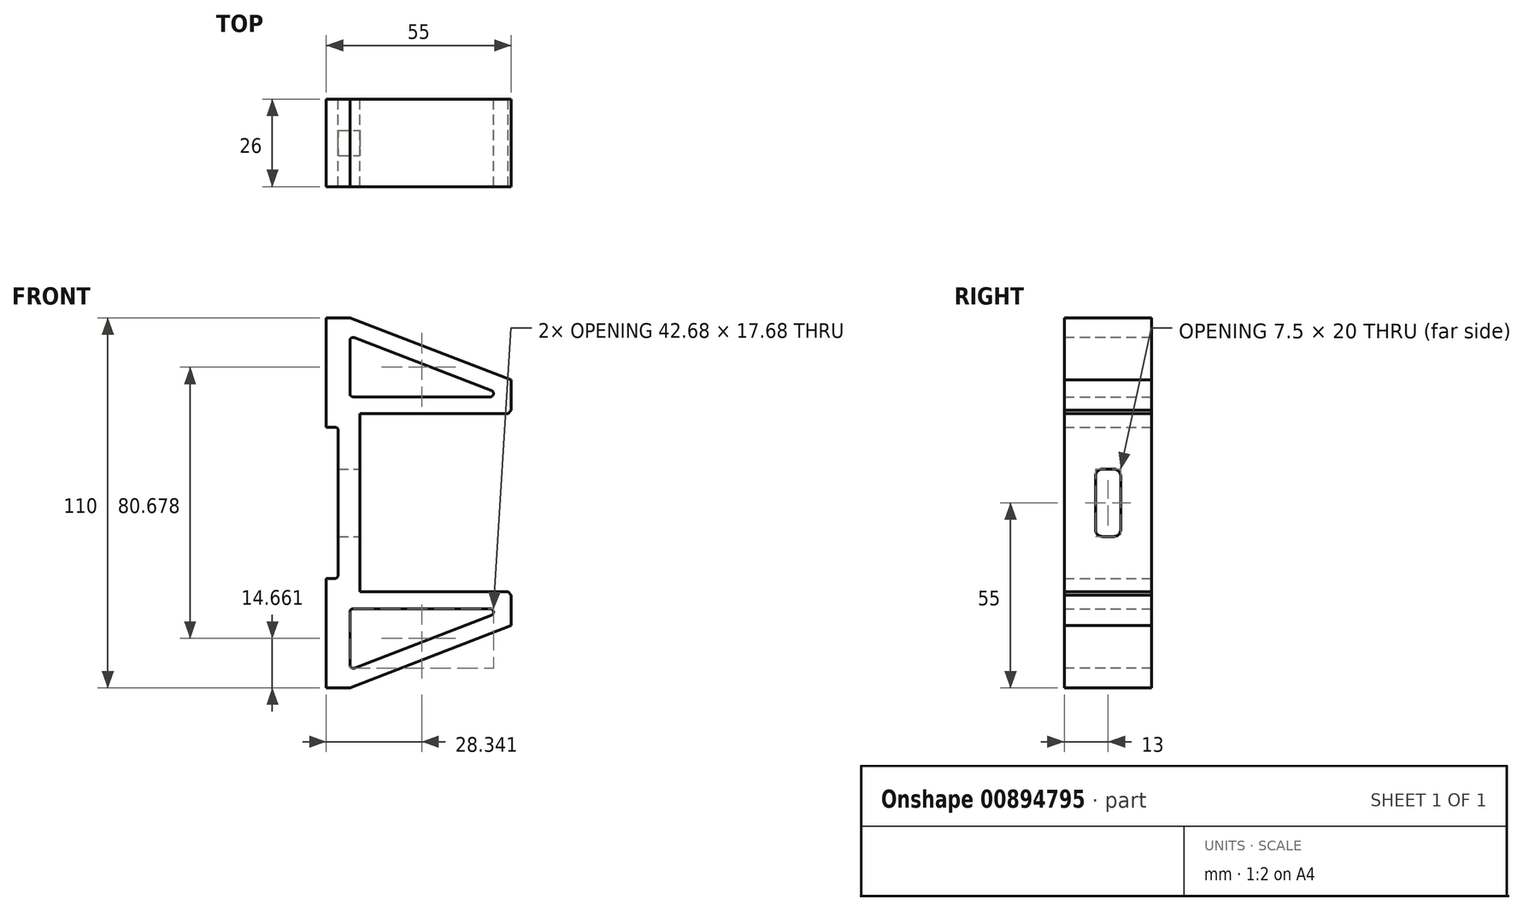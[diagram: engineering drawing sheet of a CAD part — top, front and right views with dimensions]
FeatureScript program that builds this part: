
annotation { "Feature Type Name" : "Feature", "Feature Type Description" : "" }
export const myFeature = defineFeature(function(context is Context, id is Id, definition is map)
    precondition{}
    {
        {
            var Q0;
            Q0=qCreatedBy(makeId("Front.planeOp"),FACE);
            var sketch = newSketch(context, id + "F0", { "sketchPlane" : qUnion([Q0])});
            skLineSegment(sketch, "E0.bottom", {"start": v(27.5, -55) * mm, "end": v(-27.5, -55) * mm});
            skLineSegment(sketch, "E0.top", {"start": v(27.5, 55) * mm, "end": v(-27.5, 55) * mm});
            skLineSegment(sketch, "E0.left", {"start": v(27.5, -55) * mm, "end": v(27.5, 55) * mm});
            skLineSegment(sketch, "E0.right", {"start": v(-27.5, -55) * mm, "end": v(-27.5, 55) * mm});
            skPoint(sketch, "E0.middle", {"position": v(0, 0) * mm});
            skLineSegment(sketch, "E1.bottom", {"start": v(72.5, -26.5) * mm, "end": v(-17.5, -26.5) * mm});
            skLineSegment(sketch, "E1.top", {"start": v(72.5, 26.5) * mm, "end": v(-17.5, 26.5) * mm});
            skLineSegment(sketch, "E1.left", {"start": v(72.5, -26.5) * mm, "end": v(72.5, 26.5) * mm});
            skLineSegment(sketch, "E1.right", {"start": v(-17.5, -26.5) * mm, "end": v(-17.5, 26.5) * mm});
            skPoint(sketch, "E1.middle", {"position": v(27.5, 0) * mm});
            skLineSegment(sketch, "E2", {"start": v(27.5, 36.5) * mm, "end": v(-20.5, 55) * mm});
            skLineSegment(sketch, "E3.MirrorCS", {"start": v(27.5, -36.5) * mm, "end": v(-20.5, -55) * mm});
            skLineSegment(sketch, "E4", {"start": v(-20.5, 49.64) * mm, "end": v(-20.5, 31.5) * mm});
            skLineSegment(sketch, "E5", {"start": v(26.57, 31.5) * mm, "end": v(-20.5, 49.64) * mm});
            skLineSegment(sketch, "E6", {"start": v(26.57, 31.5) * mm, "end": v(-20.5, 31.5) * mm});
            skLineSegment(sketch, "E7.MirrorCS", {"start": v(26.57, -31.5) * mm, "end": v(-20.5, -31.5) * mm});
            skLineSegment(sketch, "E8.MirrorCS", {"start": v(-20.5, -49.64) * mm, "end": v(-20.5, -31.5) * mm});
            skLineSegment(sketch, "E9.MirrorCS", {"start": v(26.57, -31.5) * mm, "end": v(-20.5, -49.64) * mm});
            skLineSegment(sketch, "E10.bottom", {"start": v(-24, 22.5) * mm, "end": v(-31, 22.5) * mm});
            skLineSegment(sketch, "E10.top", {"start": v(-24, -22.5) * mm, "end": v(-31, -22.5) * mm});
            skLineSegment(sketch, "E10.left", {"start": v(-24, 22.5) * mm, "end": v(-24, -22.5) * mm});
            skLineSegment(sketch, "E10.right", {"start": v(-31, 22.5) * mm, "end": v(-31, -22.5) * mm});
            skPoint(sketch, "E10.middle", {"position": v(-27.5, 0) * mm});
            skSolve(sketch);
        }
        {
            var Q0;
            {var subQ7=sQuery(id+"F0.wireOp",EDGE,"E0.right");Q0=makeQuery(id+"F0.imprint","IMPRINT",FACE,{"disambiguationData":[TD([[makeQuery(id+"F0.imprint","IMPRINT",EDGE,{"derivedFrom":subQ7}),-1.0]])]});}
            extrude(context, id + "F1", {"entities" : qUnion([Q0]), "depth" : 26 * mm, "offsetDistance" : 25 * mm});
        }
        {
            var Q0;
            Q0=makeQuery(id+"F1.opExtrude","SWEPT_EDGE",EDGE,{"disambiguationData":[OSD([sQuery(id+"F0.wireOp",EDGE,"E4"),sQuery(id+"F0.wireOp",EDGE,"E5")])]});
            var Q1;
            Q1=makeQuery(id+"F1.opExtrude","SWEPT_EDGE",EDGE,{"disambiguationData":[OSD([sQuery(id+"F0.wireOp",EDGE,"E4"),sQuery(id+"F0.wireOp",EDGE,"E6")])]});
            var Q2;
            Q2=makeQuery(id+"F1.opExtrude","SWEPT_EDGE",EDGE,{"disambiguationData":[OSD([sQuery(id+"F0.wireOp",EDGE,"E5"),sQuery(id+"F0.wireOp",EDGE,"E6")])]});
            var Q3;
            Q3=makeQuery(id+"F1.opExtrude","SWEPT_EDGE",EDGE,{"disambiguationData":[OSD([sQuery(id+"F0.wireOp",EDGE,"E7.MirrorCS"),sQuery(id+"F0.wireOp",EDGE,"E9.MirrorCS")])]});
            var Q4;
            Q4=makeQuery(id+"F1.opExtrude","SWEPT_EDGE",EDGE,{"disambiguationData":[OSD([sQuery(id+"F0.wireOp",EDGE,"E7.MirrorCS"),sQuery(id+"F0.wireOp",EDGE,"E8.MirrorCS")])]});
            var Q5;
            Q5=makeQuery(id+"F1.opExtrude","SWEPT_EDGE",EDGE,{"disambiguationData":[OSD([sQuery(id+"F0.wireOp",EDGE,"E8.MirrorCS"),sQuery(id+"F0.wireOp",EDGE,"E9.MirrorCS")])]});
            var Q6;
            Q6=makeQuery(id+"F1.opExtrude","SWEPT_EDGE",EDGE,{"disambiguationData":[OSD([sQuery(id+"F0.wireOp",EDGE,"E10.top"),sQuery(id+"F0.wireOp",EDGE,"E10.left")])]});
            var Q7;
            Q7=makeQuery(id+"F1.opExtrude","SWEPT_EDGE",EDGE,{"disambiguationData":[OSD([sQuery(id+"F0.wireOp",EDGE,"E10.bottom"),sQuery(id+"F0.wireOp",EDGE,"E10.left")])]});
            fillet(context, id + "F2", {"entities" : qUnion([Q0, Q1, Q2, Q3, Q4, Q5, Q6, Q7]), "radius" : 1 * mm, "tangentPropagation" : true, "allowEdgeOverflow" : false});
        }
        {
            var Q0;
            Q0=makeQuery(id+"F1.opExtrude","SWEPT_EDGE",EDGE,{"disambiguationData":[OSD([sQuery(id+"F0.wireOp",EDGE,"E0.left"),sQuery(id+"F0.wireOp",EDGE,"E1.bottom")])]});
            var Q1;
            Q1=makeQuery(id+"F1.opExtrude","SWEPT_EDGE",EDGE,{"disambiguationData":[OSD([sQuery(id+"F0.wireOp",EDGE,"E0.left"),sQuery(id+"F0.wireOp",EDGE,"E1.top")])]});
            chamfer(context, id + "F3", {"entities" : qUnion([Q0, Q1]), "width" : 1 * mm, "tangentPropagation" : true});
        }
        {
            var Q0;
            Q0=makeQuery(id+"F1.opExtrude","SWEPT_FACE",FACE,{"disambiguationData":[OSD([sQuery(id+"F0.wireOp",EDGE,"E1.right")])]});
            var sketch = newSketch(context, id + "F4", { "sketchPlane" : qUnion([Q0])});
            skLineSegment(sketch, "E11.bottom", {"start": v(-11.25, 10) * mm, "end": v(-14.75, 10) * mm});
            skLineSegment(sketch, "E11.top", {"start": v(-11.25, -10) * mm, "end": v(-14.75, -10) * mm});
            skLineSegment(sketch, "E11.left", {"start": v(-9.25, 8) * mm, "end": v(-9.25, -8) * mm});
            skLineSegment(sketch, "E11.right", {"start": v(-16.75, 8) * mm, "end": v(-16.75, -8) * mm});
            skPoint(sketch, "E11.middle", {"position": v(-13, 0) * mm});
            skPoint(sketch, "E11.middle.positionSnap0", {"position": v(-13, 26.5) * mm});
            skPoint(sketch, "E11.centerSnap0", {"position": v(-13, 26.5) * mm});
            skPoint(sketch, "E12.visualSharp", {"position": v(-9.25, 10) * mm});
            skArc(sketch, "E12.filletArc", {"start": v(-9.25, 8) * mm, "mid": v(-9.84, 9.41) * mm, "end": v(-11.25, 10) * mm});
            skPoint(sketch, "E13.visualSharp", {"position": v(-16.75, 10) * mm});
            skArc(sketch, "E13.filletArc", {"start": v(-14.75, 10) * mm, "mid": v(-16.16, 9.41) * mm, "end": v(-16.75, 8) * mm});
            skPoint(sketch, "E14.visualSharp", {"position": v(-16.75, -10) * mm});
            skArc(sketch, "E14.filletArc", {"start": v(-16.75, -8) * mm, "mid": v(-16.16, -9.41) * mm, "end": v(-14.75, -10) * mm});
            skPoint(sketch, "E15.visualSharp", {"position": v(-9.25, -10) * mm});
            skArc(sketch, "E15.filletArc", {"start": v(-11.25, -10) * mm, "mid": v(-9.84, -9.41) * mm, "end": v(-9.25, -8) * mm});
            skSolve(sketch);
        }
        {
            var Q0;
            Q0=makeQuery(id+"F4.imprint","IMPRINT",FACE,{"disambiguationData":[TD([[makeQuery(id+"F4.imprint","IMPRINT",EDGE,{"derivedFrom":sQuery(id+"F4.wireOp",EDGE,"E11.bottom")}),1.0]])]});
            extrude(context, id + "F5", {"entities" : qUnion([Q0]), "operationType" : NewBodyOperationType.REMOVE, "endBound" : BoundingType.UP_TO_NEXT, "oppositeDirection" : true, "depth" : 25 * mm, "offsetDistance" : 25 * mm});
        }
    });
